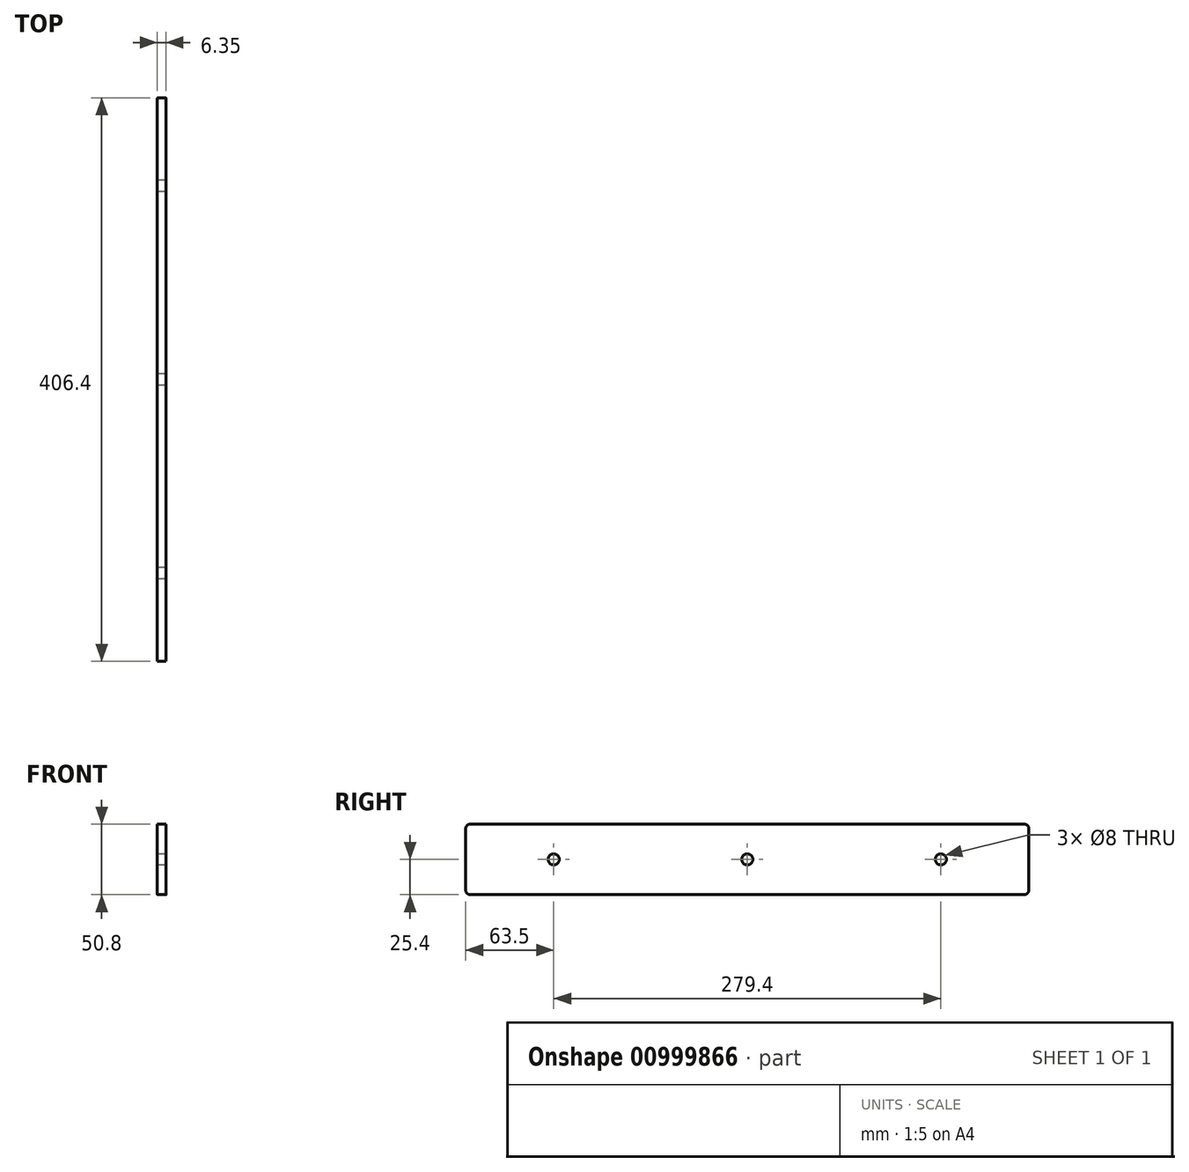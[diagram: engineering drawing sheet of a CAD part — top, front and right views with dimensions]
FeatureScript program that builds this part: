
annotation { "Feature Type Name" : "Feature", "Feature Type Description" : "" }
export const myFeature = defineFeature(function(context is Context, id is Id, definition is map)
    precondition{}
    {
        {
            var Q0;
            Q0=qCreatedBy(makeId("Right.planeOp"),FACE);
            var sketch = newSketch(context, id + "F0", { "sketchPlane" : qUnion([Q0])});
            skLineSegment(sketch, "E0.bottom", {"start": v(200.03, 25.4) * mm, "end": v(-200.03, 25.4) * mm});
            skLineSegment(sketch, "E0.top", {"start": v(200.03, -25.4) * mm, "end": v(-200.03, -25.4) * mm});
            skLineSegment(sketch, "E0.left", {"start": v(203.2, 22.23) * mm, "end": v(203.2, -22.22) * mm});
            skLineSegment(sketch, "E0.right", {"start": v(-203.2, 22.23) * mm, "end": v(-203.2, -22.22) * mm});
            skPoint(sketch, "E0.middle", {"position": v(0, 0) * mm});
            skPoint(sketch, "E1.visualSharp", {"position": v(-203.2, 25.4) * mm});
            skArc(sketch, "E1.filletArc", {"start": v(-200.03, 25.4) * mm, "mid": v(-202.27, 24.47) * mm, "end": v(-203.2, 22.23) * mm});
            skPoint(sketch, "E2.visualSharp", {"position": v(-203.2, -25.4) * mm});
            skArc(sketch, "E2.filletArc", {"start": v(-203.2, -22.22) * mm, "mid": v(-202.27, -24.47) * mm, "end": v(-200.03, -25.4) * mm});
            skPoint(sketch, "E3.visualSharp", {"position": v(203.2, -25.4) * mm});
            skArc(sketch, "E3.filletArc", {"start": v(200.03, -25.4) * mm, "mid": v(202.27, -24.47) * mm, "end": v(203.2, -22.22) * mm});
            skPoint(sketch, "E4.visualSharp", {"position": v(203.2, 25.4) * mm});
            skArc(sketch, "E4.filletArc", {"start": v(203.2, 22.23) * mm, "mid": v(202.27, 24.47) * mm, "end": v(200.03, 25.4) * mm});
            skCircle(sketch, "E5", {"center": v(0, 0) * mm, "radius": 4 * mm});
            skCircle(sketch, "E6", {"center": v(-139.7, 0) * mm, "radius": 4 * mm});
            skCircle(sketch, "E7", {"center": v(139.7, 0) * mm, "radius": 4 * mm});
            skSolve(sketch);
        }
        {
            var Q0;
            Q0=makeQuery(id+"F0.imprint","IMPRINT",FACE,{"disambiguationData":[TD([[makeQuery(id+"F0.imprint","IMPRINT",EDGE,{"derivedFrom":sQuery(id+"F0.wireOp",EDGE,"E0.bottom")}),1.0]])]});
            extrude(context, id + "F1", {"entities" : qUnion([Q0]), "depth" : 6.35 * mm, "offsetDistance" : 25.4 * mm});
        }
    });
